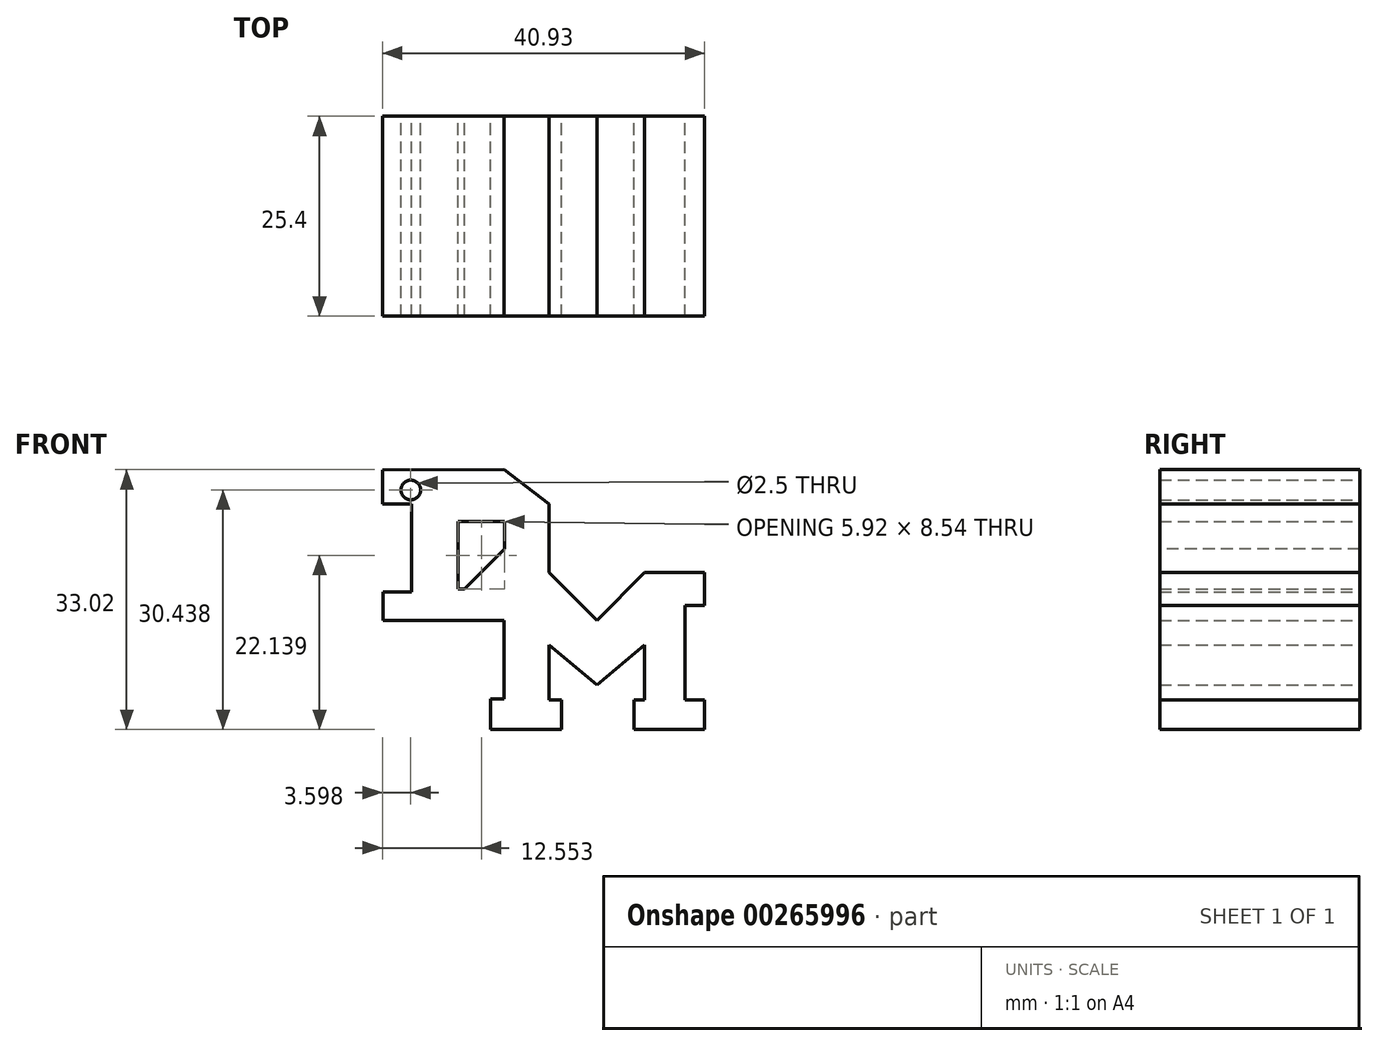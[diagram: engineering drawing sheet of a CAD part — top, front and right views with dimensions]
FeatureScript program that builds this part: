
annotation { "Feature Type Name" : "Feature", "Feature Type Description" : "" }
export const myFeature = defineFeature(function(context is Context, id is Id, definition is map)
    precondition{}
    {
        {
            var Q0;
            Q0=qCreatedBy(makeId("Front.planeOp"),FACE);
            var sketch = newSketch(context, id + "F0", { "sketchPlane" : qUnion([Q0])});
            skPoint(sketch, "E0", {"position": v(0, 0) * mm});
            skLineSegment(sketch, "E1", {"start": v(-21.16, 19.12) * mm, "end": v(-5.7, 19.16) * mm});
            skLineSegment(sketch, "E2", {"start": v(-5.7, 19.16) * mm, "end": v(0, 14.77) * mm});
            skLineSegment(sketch, "E3", {"start": v(0, 14.77) * mm, "end": v(0, 6.08) * mm});
            skLineSegment(sketch, "E4", {"start": v(0, 6.08) * mm, "end": v(-3.85, 0) * mm});
            skLineSegment(sketch, "E5", {"start": v(-3.85, 0) * mm, "end": v(-21.07, 0) * mm});
            skLineSegment(sketch, "E6", {"start": v(-21.07, 0) * mm, "end": v(-21.07, 3.61) * mm});
            skLineSegment(sketch, "E7", {"start": v(-21.07, 3.61) * mm, "end": v(-17.48, 3.61) * mm});
            skLineSegment(sketch, "E8", {"start": v(-17.48, 3.61) * mm, "end": v(-17.48, 14.77) * mm});
            skLineSegment(sketch, "E9", {"start": v(-17.48, 14.77) * mm, "end": v(-21.16, 14.77) * mm});
            skLineSegment(sketch, "E10", {"start": v(-21.16, 14.77) * mm, "end": v(-21.16, 17) * mm});
            skLineSegment(sketch, "E11", {"start": v(-11.57, 12.55) * mm, "end": v(-11.57, 4) * mm});
            skLineSegment(sketch, "E12", {"start": v(-11.57, 4) * mm, "end": v(-5.65, 4) * mm});
            skLineSegment(sketch, "E13", {"start": v(-5.65, 4) * mm, "end": v(-5.65, 12.55) * mm});
            skLineSegment(sketch, "E14", {"start": v(-5.65, 12.55) * mm, "end": v(-11.57, 12.55) * mm});
            skLineSegment(sketch, "E15", {"start": v(0, 6.08) * mm, "end": v(6.08, 0) * mm});
            skLineSegment(sketch, "E16", {"start": v(6.08, 0) * mm, "end": v(12.15, 6.08) * mm});
            skLineSegment(sketch, "E17", {"start": v(12.15, 6.08) * mm, "end": v(19.77, 6.08) * mm});
            skLineSegment(sketch, "E18", {"start": v(19.77, 6.08) * mm, "end": v(19.77, 1.94) * mm});
            skLineSegment(sketch, "E19", {"start": v(19.77, 1.94) * mm, "end": v(17.27, 1.94) * mm});
            skLineSegment(sketch, "E20", {"start": v(17.27, 1.94) * mm, "end": v(17.27, -10.1) * mm});
            skLineSegment(sketch, "E21", {"start": v(17.27, -10.1) * mm, "end": v(19.77, -10.1) * mm});
            skLineSegment(sketch, "E22", {"start": v(19.77, -10.1) * mm, "end": v(19.77, -13.86) * mm});
            skLineSegment(sketch, "E23", {"start": v(19.77, -13.86) * mm, "end": v(10.77, -13.86) * mm});
            skLineSegment(sketch, "E24", {"start": v(10.77, -13.86) * mm, "end": v(10.77, -10.1) * mm});
            skLineSegment(sketch, "E25", {"start": v(10.77, -10.1) * mm, "end": v(12.15, -10.1) * mm});
            skLineSegment(sketch, "E26", {"start": v(12.15, -10.1) * mm, "end": v(12.15, -3.08) * mm});
            skLineSegment(sketch, "E27", {"start": v(12.15, -3.08) * mm, "end": v(6.08, -8.2) * mm});
            skLineSegment(sketch, "E28", {"start": v(6.08, -8.2) * mm, "end": v(0, -3.08) * mm});
            skLineSegment(sketch, "E29", {"start": v(0, -3.08) * mm, "end": v(0, -10.1) * mm});
            skLineSegment(sketch, "E30", {"start": v(0, -10.1) * mm, "end": v(1.57, -10.1) * mm});
            skLineSegment(sketch, "E31", {"start": v(1.57, -10.1) * mm, "end": v(1.57, -13.86) * mm});
            skLineSegment(sketch, "E32", {"start": v(1.57, -13.86) * mm, "end": v(-7.42, -13.86) * mm});
            skLineSegment(sketch, "E33", {"start": v(-7.42, -13.86) * mm, "end": v(-7.42, -9.97) * mm});
            skLineSegment(sketch, "E34", {"start": v(-7.42, -9.97) * mm, "end": v(-5.72, -9.97) * mm});
            skLineSegment(sketch, "E35", {"start": v(-5.72, -9.97) * mm, "end": v(-5.72, -2.02) * mm});
            skLineSegment(sketch, "E36", {"start": v(-5.72, -2.02) * mm, "end": v(-5.72, 0) * mm});
            skLineSegment(sketch, "E37", {"start": v(-21.16, 17) * mm, "end": v(-21.16, 19.12) * mm});
            skCircle(sketch, "E38", {"center": v(-17.56, 16.58) * mm, "radius": 1.25 * mm});
            skSolve(sketch);
        }
        {
            var Q0;
            Q0=makeQuery(id+"F0.imprint","IMPRINT",FACE,{"disambiguationData":[TD([[makeQuery(id+"F0.imprint","IMPRINT",EDGE,{"derivedFrom":sQuery(id+"F0.wireOp",EDGE,"E1")}),-1.0]])]});
            var Q1;
            {var subQ2=sQuery(id+"F0.wireOp",EDGE,"E4");Q1=makeQuery(id+"F0.imprint","IMPRINT",FACE,{"disambiguationData":[TD([[makeQuery(id+"F0.imprint","IMPRINT",EDGE,{"derivedFrom":subQ2}),1.0]])]});}
            extrude(context, id + "F1", {"entities" : qUnion([Q0, Q1]), "endBound" : BoundingType.SYMMETRIC, "depth" : 25.4 * mm});
        }
        {
            var Q0;
            Q0=makeQuery(id+"F1.opExtrude","SWEPT_EDGE",EDGE,{"disambiguationData":[OSD([sQuery(id+"F0.wireOp",EDGE,"E12"),sQuery(id+"F0.wireOp",EDGE,"E13")])]});
            chamfer(context, id + "F2", {"entities" : qUnion([Q0]), "width" : 5.08 * mm, "tangentPropagation" : true});
        }
    });
